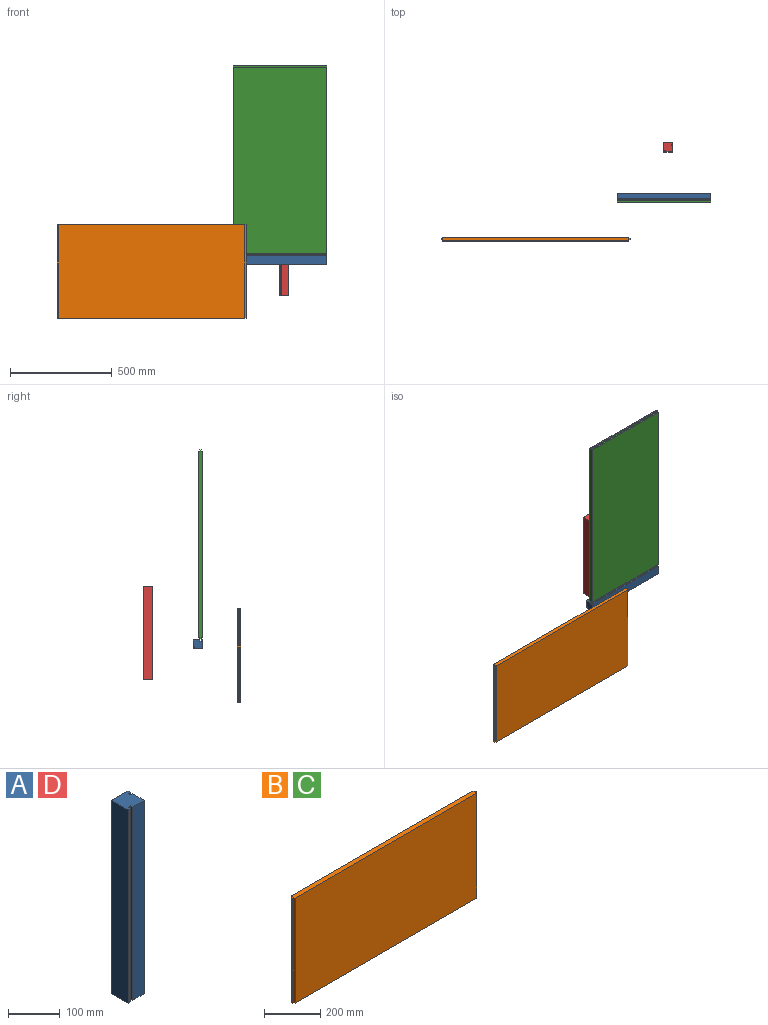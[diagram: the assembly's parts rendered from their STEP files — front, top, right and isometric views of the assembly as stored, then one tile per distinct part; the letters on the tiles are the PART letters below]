
ASSEMBLY  parts=4 mates=1
PART A: 14 faces, bbox 44.5x44.5x457.2 mm
  f0: plane 457.2x6.35mm, normal (0,-1,0), area 2903.2mm2, adj f1,f11,f12,f13
  f1: plane 457.2x6.35mm, normal (1,0,0), area 2903.2mm2, adj f0,f2,f12,f13
  f2: plane 457.2x6.35mm, normal (0,-1,0), area 2903.2mm2, adj f1,f3,f12,f13
  f3: plane 457.2x6.35mm, normal (-1,0,0), area 2903.2mm2, adj f2,f4,f12,f13
  f4: plane 457.2x31.75mm, normal (0,-1,0), area 14516.1mm2, adj f3,f5,f12,f13
  f5: plane 457.2x31.75mm, normal (1,0,0), area 14516.1mm2, adj f4,f6,f12,f13
  f6: plane 457.2x6.35mm, normal (0,1,0), area 2903.2mm2, adj f5,f7,f12,f13
  f7: plane 457.2x6.35mm, normal (1,0,0), area 2903.2mm2, adj f6,f8,f12,f13
  f8: plane 457.2x6.35mm, normal (0,-1,0), area 2903.2mm2, adj f7,f9,f12,f13
  f9: plane 457.2x6.35mm, normal (1,0,0), area 2903.2mm2, adj f8,f10,f12,f13
  f10: plane 457.2x44.45mm, normal (0,1,0), area 20322.5mm2, adj f9,f11,f12,f13
  f11: plane 457.2x44.45mm, normal (-1,0,0), area 20322.5mm2, adj f0,f10,f12,f13
  f12: plane 44.45x44.45mm, normal (0,0,1), area 1895.2mm2, adj f0,f1,f2,f3,f4,f5,f6,f7
  f13: plane 44.45x44.45mm, normal (0,0,-1), area 1895.2mm2, adj f0,f1,f2,f3,f4,f5,f6,f7
PART B: 14 faces, bbox 927.1x19.1x457.2 mm
  f0: plane 914.4x457.2mm, normal (0,1,0), area 418063.7mm2, adj f1,f11,f12,f13
  f1: plane 457.2x6.35mm, normal (-1,0,0), area 2903.2mm2, adj f0,f2,f12,f13
  f2: plane 457.2x6.35mm, normal (0,1,0), area 2903.2mm2, adj f1,f3,f12,f13
  f3: plane 457.2x6.35mm, normal (-1,0,0), area 2903.2mm2, adj f2,f4,f12,f13
  f4: plane 457.2x6.35mm, normal (0,-1,0), area 2903.2mm2, adj f3,f5,f12,f13
  f5: plane 457.2x6.35mm, normal (-1,0,0), area 2903.2mm2, adj f4,f6,f12,f13
  f6: plane 914.4x457.2mm, normal (0,-1,0), area 418063.7mm2, adj f5,f7,f12,f13
  f7: plane 457.2x6.35mm, normal (1,0,0), area 2903.2mm2, adj f6,f8,f12,f13
  f8: plane 457.2x6.35mm, normal (0,-1,0), area 2903.2mm2, adj f7,f9,f12,f13
  f9: plane 457.2x6.35mm, normal (1,0,0), area 2903.2mm2, adj f8,f10,f12,f13
  f10: plane 457.2x6.35mm, normal (0,1,0), area 2903.2mm2, adj f9,f11,f12,f13
  f11: plane 457.2x6.35mm, normal (1,0,0), area 2903.2mm2, adj f0,f10,f12,f13
  f12: plane 927.1x19.05mm, normal (0,0,1), area 17500mm2, adj f0,f1,f2,f3,f4,f5,f6,f7
  f13: plane 927.1x19.05mm, normal (0,0,-1), area 17500mm2, adj f0,f1,f2,f3,f4,f5,f6,f7
PART C: same geometry as B
PART D: same geometry as A
PLACE A rot(axis=(-0.58,-0.58,0.58),120deg) t=(877.47,248.58,162.9)mm
PLACE B t=(-437.48,72.19,-142.16)mm fixed
PLACE C rot(axis=(0,1,0),90deg) t=(420.27,261.59,1089.52)mm
PLACE D t=(645.54,495.93,-29.67)mm
MATE planar C.f12 <-> A.f13  axis (1,0,0) through (877.47,248.89,175.12)mm
